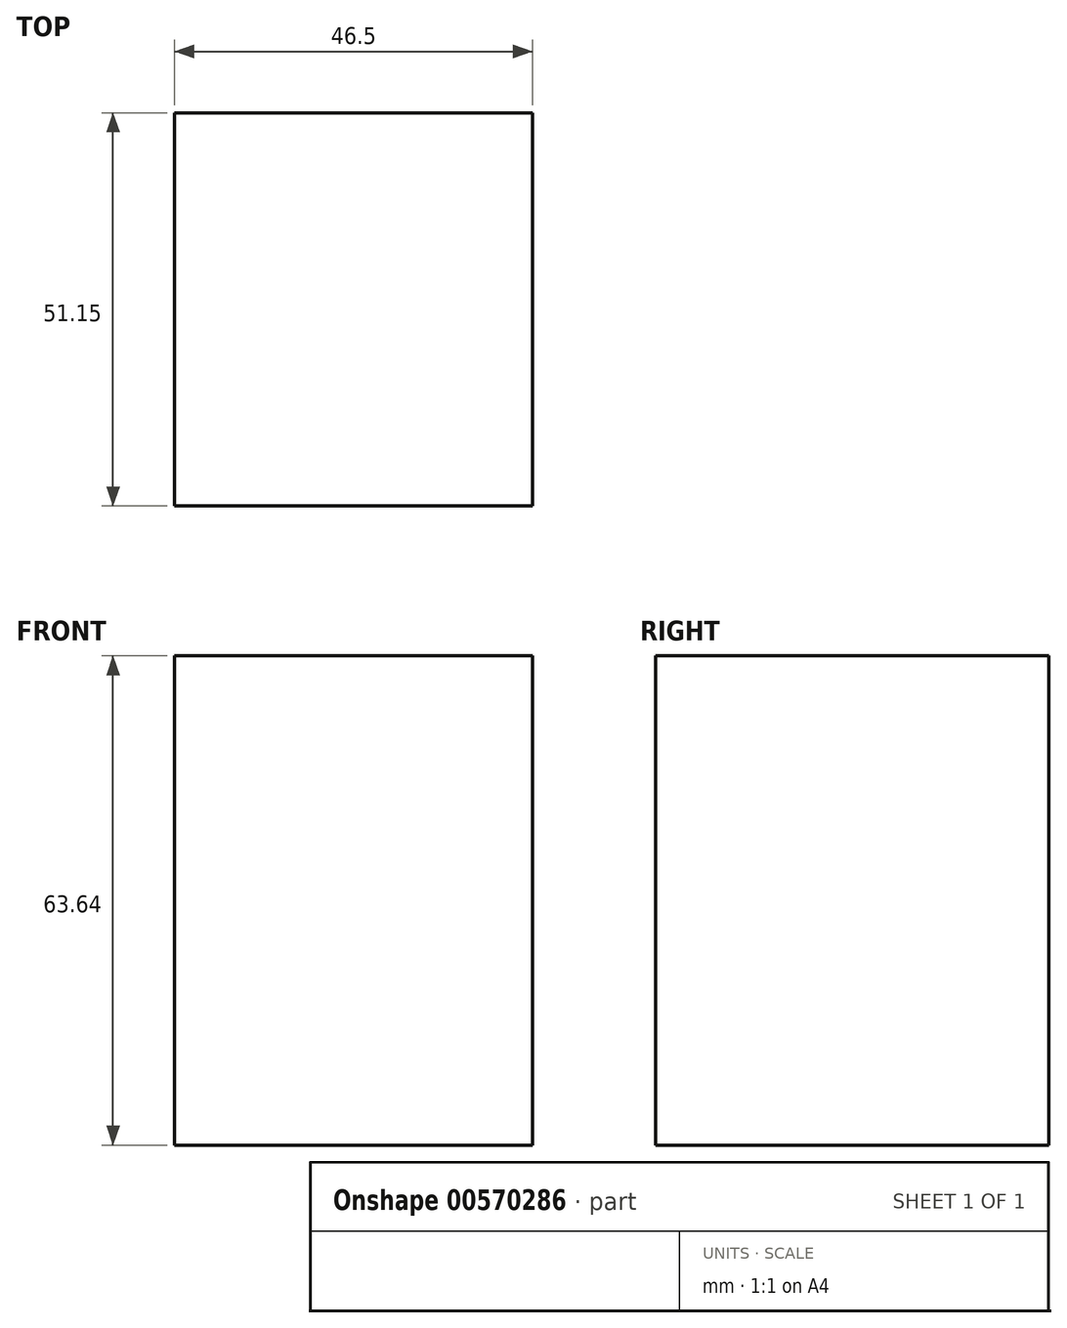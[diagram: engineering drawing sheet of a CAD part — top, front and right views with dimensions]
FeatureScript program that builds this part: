
annotation { "Feature Type Name" : "Feature", "Feature Type Description" : "" }
export const myFeature = defineFeature(function(context is Context, id is Id, definition is map)
    precondition{}
    {
        {
            var Q0;
            Q0=qCreatedBy(makeId("Top.planeOp"),FACE);
            var sketch = newSketch(context, id + "F0", { "sketchPlane" : qUnion([Q0])});
            skLineSegment(sketch, "E0.bottom", {"start": v(-21.75, 24.15) * mm, "end": v(24.75, 24.15) * mm});
            skLineSegment(sketch, "E0.top", {"start": v(-21.75, -27) * mm, "end": v(24.75, -27) * mm});
            skLineSegment(sketch, "E0.left", {"start": v(-21.75, 24.15) * mm, "end": v(-21.75, -27) * mm});
            skLineSegment(sketch, "E0.right", {"start": v(24.75, 24.15) * mm, "end": v(24.75, -27) * mm});
            skSolve(sketch);
        }
        {
            var Q0;
            Q0=makeQuery(id+"F0.imprint","IMPRINT",FACE,{"disambiguationData":[TD([[makeQuery(id+"F0.imprint","IMPRINT",EDGE,{"derivedFrom":sQuery(id+"F0.wireOp",EDGE,"E0.bottom")}),-1.0]])]});
            extrude(context, id + "F1", {"entities" : qUnion([Q0]), "depth" : 63.64 * mm, "offsetDistance" : 25.4 * mm});
        }
    });
